# Revit family: DLB070014
name_source: partatom
category: Appareils sanitaires
revit_build: Autodesk Revit 2015 (Build: 20140606_1530(x64)
units: mm (PartAtom-declared; Revit-internal decimal feet)

## types (1)
- DLB070014
    Category = WC
    Commentaires du type = Washbasin and hung WC combination
    Description = French manufacturer Delabie is a leader in the European sanitary ware market for non-domestic places. Water controls, solutions for disabled people, sanitary ware, for schools, leisure centres, offices, hospitals, airports…
    Fabricant = DELABIE
    Features  = Combination unit: washbasin and floor-standing WC pan with recessed toilet roll holder.
Service duct installation (through-the-wall).
WC pan on the right hand side to the unit.
Bacteriostatic 304 stainless steel.
Stainless steel unit thickness: 2mm.
Rounded corners and edges for improved safety.
Smooth surface for easy cleaning.
Suitable for prisons, police stations, etc.
WC pan is completely welded to washbasin, no screws: makes cleaning easier and prevents concealment of objects.
Washbasin equipped with time flow tap: stainless steel tamperproof push-button and anti-blocking system, 7 second time flow, M½".
WC equipped with time flow flush valve, 7 second time flow, M¾".
Water inlet: washbasin M½", WC M¾".
Recessed horizontal water outlet: Ø 100mm.
200mm threaded rod can be cut to size (other lengths available on request).
Easy installation: only one water outlet for both washbasin and WC, water inlet and outlet already connected.
Weight: 30kg.
    Finish = Polished satin
    Grade = CE
    ManufacturerName = DELABIE
    ManufacturerURL = http://www.delabie.com
    Material = 304 stainless steel
    ModelNumber = 166600
    Modèle = KOMPACT TC washbasin and hung WC combination
    Name = KOMPACT TC washbasin and hung WC combination
    NominalHeight = 1000 mm  [stored 3.28084 ft]
    NominalLength = 725 mm  [stored 2.37861 ft]
    NominalWidth = 615 mm  [stored 2.01772 ft]
    ProductInformation = http://www.delabie.com
    Radius (Washbasin) = 10 mm  [stored 0.0328084 ft]
    Radius (in WC) = 13 mm
    Radius (out WC) = 50 mm  [stored 0.164042 ft]
    SerialNumber = 3456330154116
    URL = http://www.delabie.com
    Version = v1
    WarrantyDescription = Any manufacturing defect
    WarrantyDurationUnit = 10 years
    Weight = 30kg

note: [stored X ft] marks values corroborated as IEEE doubles in the binary element streams (Revit-internal decimal feet)

## geometry (parser evidence)
native form markers: Blend x30, Sweep x8
no freeform markers — native parametric forms only
